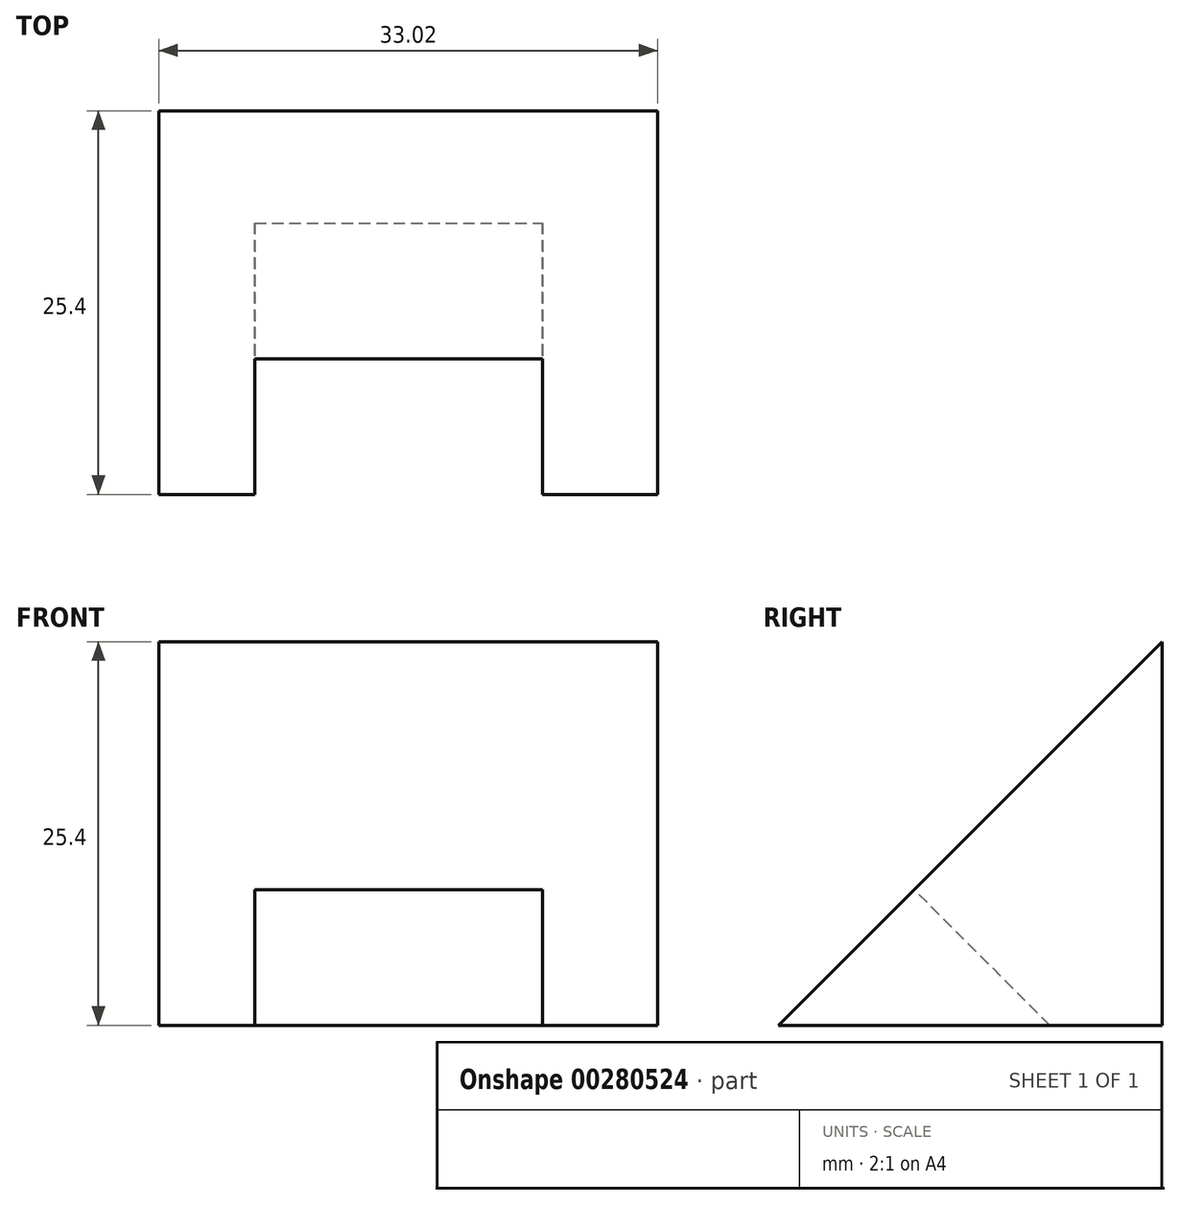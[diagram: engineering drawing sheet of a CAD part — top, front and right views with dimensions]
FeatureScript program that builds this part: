
annotation { "Feature Type Name" : "Feature", "Feature Type Description" : "" }
export const myFeature = defineFeature(function(context is Context, id is Id, definition is map)
    precondition{}
    {
        {
            var Q0;
            Q0=qCreatedBy(makeId("Front.planeOp"),FACE);
            var sketch = newSketch(context, id + "F0", { "sketchPlane" : qUnion([Q0])});
            skLineSegment(sketch, "E0.bottom", {"start": v(0, 0) * mm, "end": v(33.02, 0) * mm});
            skLineSegment(sketch, "E0.top", {"start": v(0, 25.4) * mm, "end": v(33.02, 25.4) * mm});
            skLineSegment(sketch, "E0.left", {"start": v(0, 0) * mm, "end": v(0, 25.4) * mm});
            skLineSegment(sketch, "E0.right", {"start": v(33.02, 0) * mm, "end": v(33.02, 25.4) * mm});
            skSolve(sketch);
        }
        {
            var Q0;
            Q0=makeQuery(id+"F0.imprint","IMPRINT",FACE,{"disambiguationData":[TD([[makeQuery(id+"F0.imprint","IMPRINT",EDGE,{"derivedFrom":sQuery(id+"F0.wireOp",EDGE,"E0.bottom")}),1.0]])]});
            extrude(context, id + "F1", {"entities" : qUnion([Q0]), "endBound" : BoundingType.SYMMETRIC, "depth" : 25.4 * mm});
        }
        {
            var Q0;
            Q0=makeQuery(id+"F1.opExtrude","SWEPT_FACE",FACE,{"disambiguationData":[OSD([sQuery(id+"F0.wireOp",EDGE,"E0.right")])]});
            var sketch = newSketch(context, id + "F2", { "sketchPlane" : qUnion([Q0])});
            skLineSegment(sketch, "E1", {"start": v(12.7, 25.4) * mm, "end": v(-12.7, 0) * mm});
            skLineSegment(sketch, "E2", {"start": v(-12.7, 0) * mm, "end": v(-12.7, 25.4) * mm});
            skLineSegment(sketch, "E3", {"start": v(-12.7, 25.4) * mm, "end": v(12.7, 25.4) * mm});
            skSolve(sketch);
        }
        {
            var Q0;
            Q0=makeQuery(id+"F2.imprint","IMPRINT",FACE,{"disambiguationData":[TD([[makeQuery(id+"F2.imprint","IMPRINT",EDGE,{"derivedFrom":sQuery(id+"F2.wireOp",EDGE,"E1")}),-1.0]])]});
            extrude(context, id + "F3", {"entities" : qUnion([Q0]), "operationType" : NewBodyOperationType.REMOVE, "endBound" : BoundingType.THROUGH_ALL, "oppositeDirection" : true, "depth" : 25.4 * mm});
        }
        {
            var Q0;
            Q0=makeQuery(id+"F3.boolean.opBoolean","COPY",FACE,{"derivedFrom":makeQuery(id+"F3.opExtrude","SWEPT_FACE",FACE,{"disambiguationData":[OSD([sQuery(id+"F2.wireOp",EDGE,"E1")])]})});
            var sketch = newSketch(context, id + "F4", { "sketchPlane" : qUnion([Q0])});
            skLineSegment(sketch, "E4.bottom", {"start": v(6.35, -8.98) * mm, "end": v(25.4, -8.98) * mm});
            skLineSegment(sketch, "E4.top", {"start": v(6.35, 3.72) * mm, "end": v(25.4, 3.72) * mm});
            skLineSegment(sketch, "E4.left", {"start": v(6.35, -8.98) * mm, "end": v(6.35, 3.72) * mm});
            skLineSegment(sketch, "E4.right", {"start": v(25.4, -8.98) * mm, "end": v(25.4, 3.72) * mm});
            skSolve(sketch);
        }
        {
            var Q0;
            Q0=makeQuery(id+"F4.imprint","IMPRINT",FACE,{"disambiguationData":[TD([[makeQuery(id+"F4.imprint","IMPRINT",EDGE,{"derivedFrom":sQuery(id+"F4.wireOp",EDGE,"E4.bottom")}),1.0]])]});
            extrude(context, id + "F5", {"entities" : qUnion([Q0]), "operationType" : NewBodyOperationType.REMOVE, "oppositeDirection" : true, "depth" : 12.7 * mm});
        }
    });
